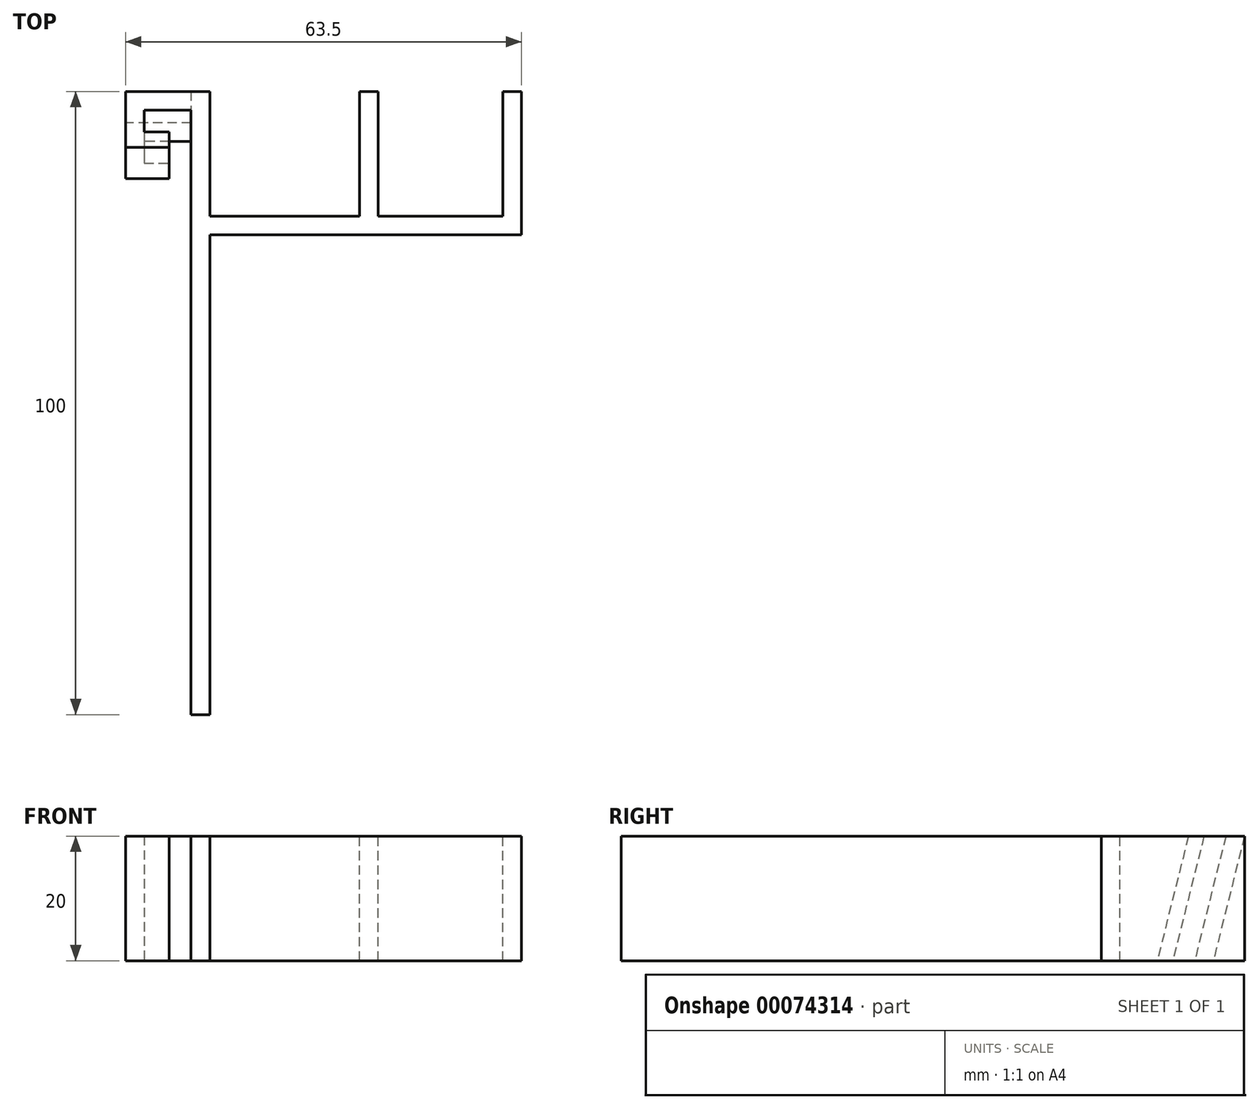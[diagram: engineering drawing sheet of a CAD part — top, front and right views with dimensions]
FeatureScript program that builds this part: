
annotation { "Feature Type Name" : "Feature", "Feature Type Description" : "" }
export const myFeature = defineFeature(function(context is Context, id is Id, definition is map)
    precondition{}
    {
        {
            var Q0;
            Q0=qCreatedBy(makeId("Top.planeOp"),FACE);
            var sketch = newSketch(context, id + "F0", { "sketchPlane" : qUnion([Q0])});
            skLineSegment(sketch, "E0.rect.bottom", {"start": v(-1.5, 50) * mm, "end": v(1.5, 50) * mm});
            skLineSegment(sketch, "E0.rect.top", {"start": v(-1.5, -50) * mm, "end": v(1.5, -50) * mm});
            skLineSegment(sketch, "E0.rect.left", {"start": v(-1.5, 50) * mm, "end": v(-1.5, -50) * mm});
            skLineSegment(sketch, "E0.rect.right", {"start": v(1.5, 50) * mm, "end": v(1.5, 30) * mm});
            skPoint(sketch, "E0.rect.middle", {"position": v(0, 0) * mm});
            skLineSegment(sketch, "E1.bottom", {"start": v(1.5, 30) * mm, "end": v(25.5, 30) * mm});
            skLineSegment(sketch, "E1.top", {"start": v(1.5, 27) * mm, "end": v(51.5, 27) * mm});
            skLineSegment(sketch, "E1.right", {"start": v(51.5, 30) * mm, "end": v(51.5, 27) * mm});
            skLineSegment(sketch, "E2.top", {"start": v(51.5, 50) * mm, "end": v(48.5, 50) * mm});
            skLineSegment(sketch, "E2.left", {"start": v(51.5, 30) * mm, "end": v(51.5, 50) * mm});
            skLineSegment(sketch, "E2.right", {"start": v(48.5, 30) * mm, "end": v(48.5, 50) * mm});
            skLineSegment(sketch, "E3.top", {"start": v(28.5, 50) * mm, "end": v(25.5, 50) * mm});
            skLineSegment(sketch, "E3.left", {"start": v(28.5, 30) * mm, "end": v(28.5, 50) * mm});
            skLineSegment(sketch, "E3.right", {"start": v(25.5, 30) * mm, "end": v(25.5, 50) * mm});
            skLineSegment(sketch, "E4.trimOffspring", {"start": v(1.5, 27) * mm, "end": v(1.5, -50) * mm});
            skLineSegment(sketch, "E5.trimOffspring", {"start": v(28.5, 30) * mm, "end": v(48.5, 30) * mm});
            skLineSegment(sketch, "E6.bottom", {"start": v(-1.5, 50) * mm, "end": v(-12, 50) * mm});
            skLineSegment(sketch, "E6.top", {"start": v(-1.5, 47) * mm, "end": v(-9, 47) * mm});
            skLineSegment(sketch, "E6.left", {"start": v(-1.5, 50) * mm, "end": v(-1.5, 47) * mm});
            skLineSegment(sketch, "E6.right", {"start": v(-12, 50) * mm, "end": v(-12, 47) * mm});
            skLineSegment(sketch, "E7.top", {"start": v(-12, 41) * mm, "end": v(-9, 41) * mm});
            skLineSegment(sketch, "E7.left", {"start": v(-12, 47) * mm, "end": v(-12, 41) * mm});
            skLineSegment(sketch, "E7.right", {"start": v(-9, 47) * mm, "end": v(-9, 43.5) * mm});
            skLineSegment(sketch, "E8.bottom", {"start": v(-9, 41) * mm, "end": v(-5, 41) * mm});
            skLineSegment(sketch, "E8.top", {"start": v(-9, 43.5) * mm, "end": v(-5, 43.5) * mm});
            skLineSegment(sketch, "E8.right", {"start": v(-5, 41) * mm, "end": v(-5, 43.5) * mm});
            skPoint(sketch, "E9", {"position": v(-1.5, 48.5) * mm});
            skSolve(sketch);
        }
        {
            var Q0;
            Q0=makeQuery(id+"F0.imprint","IMPRINT",FACE,{"disambiguationData":[TD([[makeQuery(id+"F0.imprint","IMPRINT",EDGE,{"derivedFrom":sQuery(id+"F0.wireOp",EDGE,"E0.rect.bottom")}),-1.0]])]});
            extrude(context, id + "F1", {"entities" : qUnion([Q0]), "oppositeDirection" : true, "depth" : 20 * mm});
        }
        {
            var Q0;
            Q0=makeQuery(id+"F1.opExtrude","SWEPT_FACE",FACE,{"disambiguationData":[OSD([sQuery(id+"F0.wireOp",EDGE,"E0.rect.left"),sQuery(id+"F0.wireOp",EDGE,"E6.left")])]});
            var sketch = newSketch(context, id + "F2", { "sketchPlane" : qUnion([Q0])});
            skLineSegment(sketch, "E10", {"start": v(-48.5, 0) * mm, "end": v(-43.5, -20) * mm});
            skSolve(sketch);
        }
        {
            var Q0;
            Q0=makeQuery(id+"F0.imprint","IMPRINT",FACE,{"disambiguationData":[TD([[makeQuery(id+"F0.imprint","IMPRINT",EDGE,{"derivedFrom":sQuery(id+"F0.wireOp",EDGE,"E6.bottom")}),1.0]])]});
            var Q1;
            Q1=sQuery(id+"F2.wireOp",EDGE,"E10");
            sweep(context, id + "F3", {"operationType" : NewBodyOperationType.ADD, "profiles" : qUnion([Q0]), "path" : qUnion([Q1])});
        }
    });
